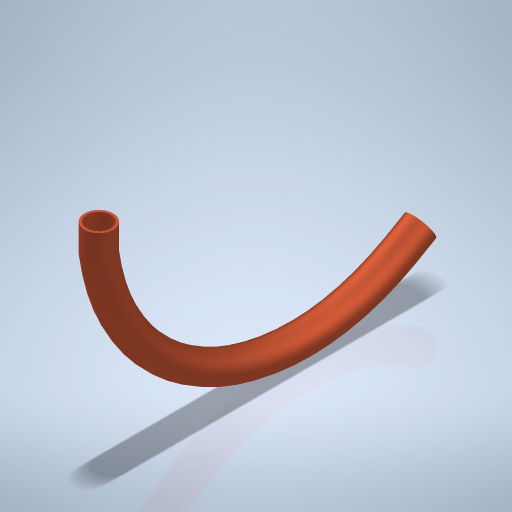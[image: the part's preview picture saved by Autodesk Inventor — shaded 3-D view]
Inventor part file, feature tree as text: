
AUTODESK INVENTOR PART (.ipt)
format: ipt  version: 2024 (Build 280153000, 153)  size: 309,248 bytes
history: native  units: mm
features: sketch x4, plane x1, sweep x1, shell x1
ambient origin geometry x8: Origin, YZ Plane, XZ Plane, XY Plane, X Axis, Y Axis, Z Axis, Center Point
bodies: Body1 (feature_tree)
feature tree (7):
  sketch  "Skizze1"  dims[d0=5.0mm d1=5.5mm d2=-5.5mm]
  sketch  "Skizze2"  dims[d3=6.0mm]
  plane  "Arbeitsebene1"
  sweep  "Sweeping1"
  shell  "Wandung1"  Thickness=-5.5mm
  sketch  "Skizze3"  dims[d4=42.3mm]
  sketch  "Skizze4"  dims[d5=4.7mm d10=0.0mm d11=0.0mm d12=0.5mm d13=60.0deg]
